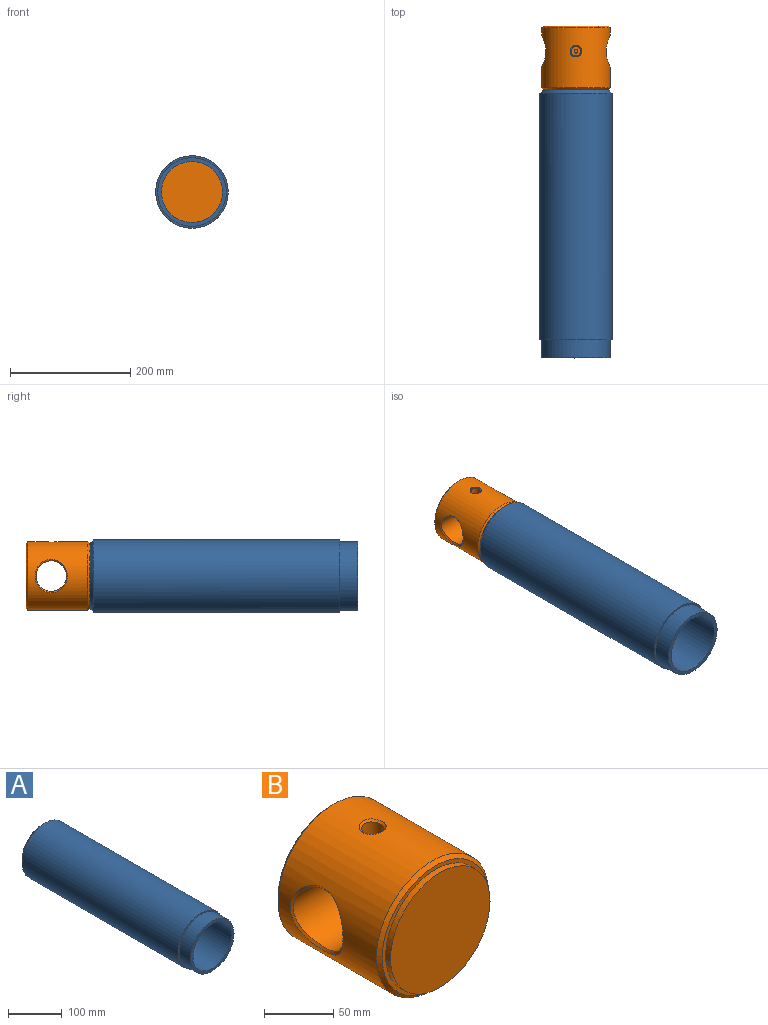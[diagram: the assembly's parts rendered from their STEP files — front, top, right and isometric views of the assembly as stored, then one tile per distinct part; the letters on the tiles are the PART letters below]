
ASSEMBLY  parts=2 mates=1
PART A: 7 faces, bbox 120.7x447x120.7 mm
  f0: cylinder r=60.32mm len=411mm, axis (0,1,0), area 155782.6mm2, adj f4,f6
  f1: plane 114.3x114.3mm, normal (0,-1,0), area 2153.5mm2, adj f2,f5
  f2: cylinder r=50.8mm len=447mm, axis (0,1,0), area 142676.1mm2, adj f1,f3
  f3: plane 108.65x108.65mm, normal (0,1,0), area 1164.2mm2, adj f2,f4
  f4: cone r=60.32mm half-angle=45deg, axis (0,-1,0), area 3056.3mm2, adj f0,f3
  f5: cylinder r=57.15mm len=114.3mm, axis (0,-1,0), area 10772.5mm2, adj f1,f6
  f6: plane 120.65x120.65mm, normal (0,-1,0), area 1171.8mm2, adj f0,f5
PART B: 14 faces, bbox 114.5x111x114.5 mm
  f0: cylinder r=3mm len=14.6mm, axis (0,0,-1), area 275.2mm2, adj f2,f10
  f1: cylinder r=57.25mm len=114.5mm, axis (0,1,0), area 31011.8mm2, adj f7,f8,f11,f12,f13
  f2: cylinder r=25.4mm len=111.4mm, axis (1,0,0), area 16681.5mm2, adj f0,f11,f13
  f3: plane 108.5x108.5mm, normal (0,-1,0), area 1138.6mm2, adj f5,f7
  f4: plane 109.5x109.5mm, normal (0,1,0), area 9417.1mm2, adj f8
  f5: cylinder r=50.8mm len=101.6mm, axis (0,1,0), area 1595.9mm2, adj f3,f6
  f6: plane 101.6x101.6mm, normal (0,-1,0), area 8107.3mm2, adj f5
  f7: cone r=54.25mm half-angle=45deg, axis (0,1,0), area 1486.1mm2, adj f1,f3
  f8: cone r=57.25mm half-angle=45deg, axis (0,-1,0), area 1244mm2, adj f1,f4
  f9: cylinder r=8mm len=16mm, axis (0,0,-1), area 789.1mm2, adj f10,f12
  f10: plane 16x16mm, normal (0,0,1), area 172.8mm2, adj f0,f9
  f11: bspline ~55.41x53.91mm, area 411.2mm2, adj f1,f2
  f12: bspline ~19.64x19.11mm, area 127.2mm2, adj f1,f9
  f13: bspline ~55.41x53.91mm, area 411.2mm2, adj f1,f2
PLACE A t=(-197.82,-17.52,-70.96)mm
PLACE B t=(-197.82,93.48,-70.96)mm
MATE fastened A.f0 <-> B.f1  axis (0,1,0) through (-197.82,-12.52,-70.96)mm
